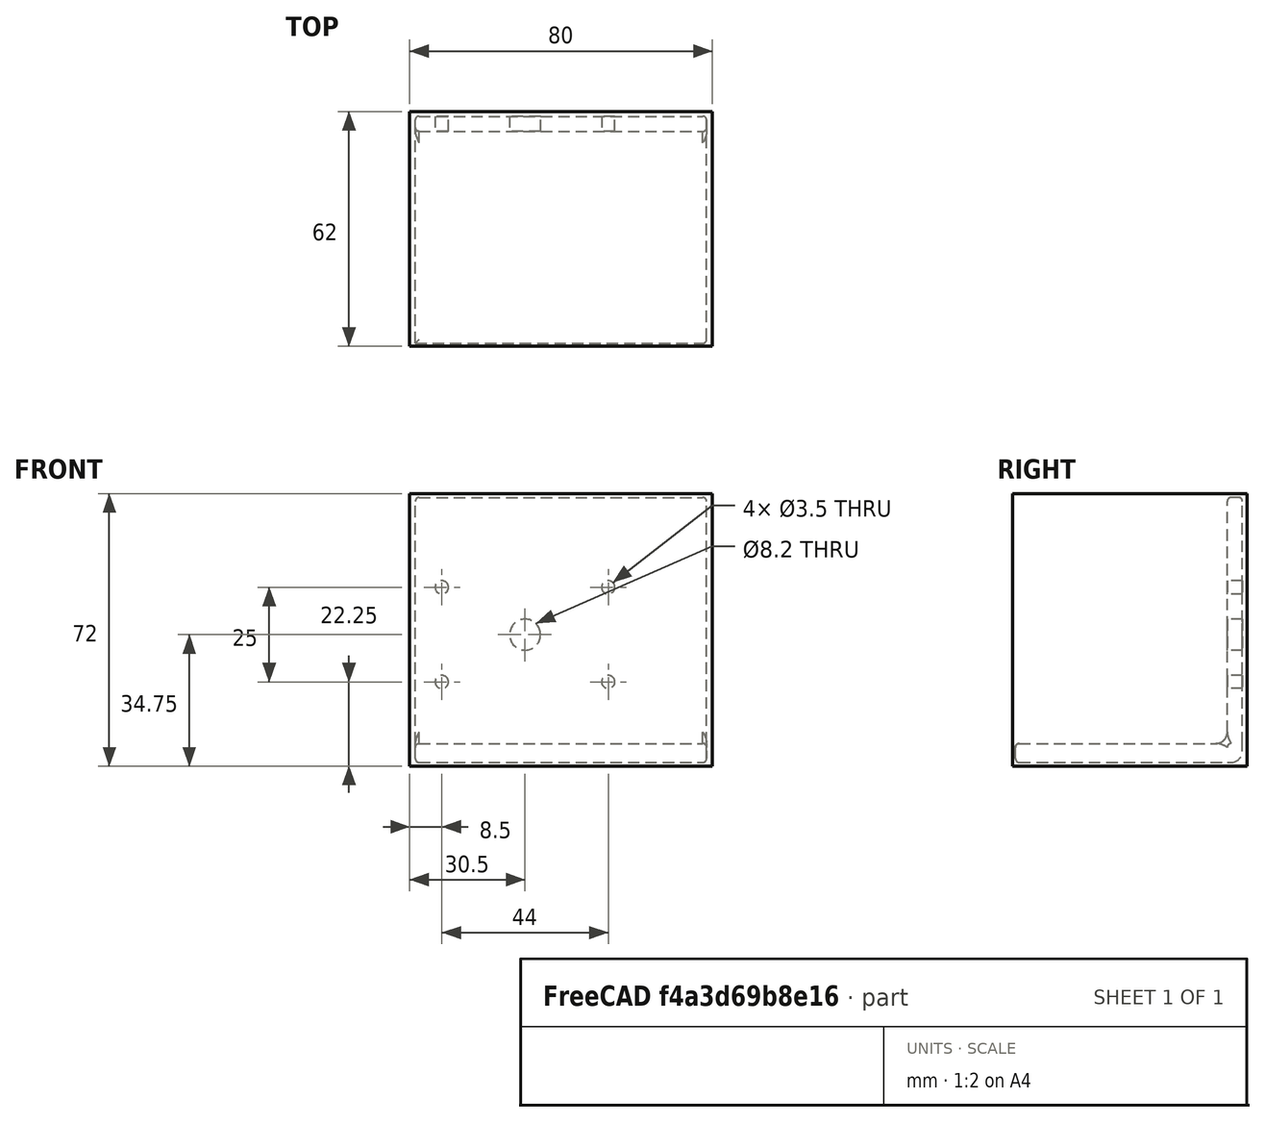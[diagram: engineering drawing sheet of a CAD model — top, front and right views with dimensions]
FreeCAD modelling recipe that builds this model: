
FCSTD DOCUMENT  (FreeCAD 0.21R33668 +7 (Git))
Label: OPC_N3_Base_July_10_2024
License: All rights reserved
LicenseURL: https://en.wikipedia.org/wiki/All_rights_reserved
objects: Part::Cylinder×5, Part::Box×3, Part::MultiFuse×2, Mesh::Feature×1, Part::Cut×1, Part::Fillet×1
note: 12 computed .brp shape members not serialized (recipe doc carries the construction recipe); baked Part::Feature solids carry a one-line shape summary decoded from their .brp

FEATURE [Mesh::Feature] opc_n3
FEATURE [Part::Box] Box  label="Horizontal"
  AttacherType = Attacher::AttachEngine3D
  Height = 5
  Length = 77
  Placement = pos=(-2.5,-31.25,-37) rot=(0,0,1;0rad)
  Width = 60
FEATURE [Part::Box] Box001  label="Vertical"
  AttacherType = Attacher::AttachEngine3D
  Height = 4
  Length = 77
  Placement = pos=(-2.5,28.75,-37) rot=(1,0,0;1.5708rad)
  Width = 70
FEATURE [Part::MultiFuse] Fusion  label="Plate"
  Shapes = -> [Box,Box001]
FEATURE [Part::Cylinder] Cylinder
  Angle = 360
  AttacherType = Attacher::AttachEngine3D
  FirstAngle = 0
  Height = 10
  Placement = pos=(26.5,22,-3.25) rot=(1,0,0;4.71239rad)
  Radius = 4.1
  SecondAngle = 0
FEATURE [Part::Cylinder] Cylinder001
  Angle = 360
  AttacherType = Attacher::AttachEngine3D
  FirstAngle = 0
  Height = 10
  Placement = pos=(48.5,22,9.25) rot=(-1,0,0;1.5708rad)
  Radius = 1.75
  SecondAngle = 0
FEATURE [Part::Cylinder] Cylinder003
  Angle = 360
  AttacherType = Attacher::AttachEngine3D
  FirstAngle = 0
  Height = 10
  Placement = pos=(4.5,22,-15.75) rot=(-1,0,0;1.5708rad)
  Radius = 1.75
  SecondAngle = 0
FEATURE [Part::Cylinder] Cylinder002
  Angle = 360
  AttacherType = Attacher::AttachEngine3D
  FirstAngle = 0
  Height = 10
  Placement = pos=(4.5,22,9.25) rot=(-1,0,0;1.5708rad)
  Radius = 1.75
  SecondAngle = 0
FEATURE [Part::Cylinder] Cylinder004
  Angle = 360
  AttacherType = Attacher::AttachEngine3D
  FirstAngle = 0
  Height = 10
  Placement = pos=(48.5,22,-15.75) rot=(-1,0,0;1.5708rad)
  Radius = 1.75
  SecondAngle = 0
FEATURE [Part::MultiFuse] Fusion001  label="Holes"
  Shapes = -> [Cylinder,Cylinder001,Cylinder002,Cylinder003,Cylinder004]
FEATURE [Part::Cut] Cut  label="Mount_Plate"
  Base = -> Fusion
  Tool = -> Fusion001
FEATURE [Part::Fillet] Fillet  label="MountPlate"
  Base = -> Cut
  Edges = 17 edges: [Edge1 r=1,Edge3 r=1,Edge5 r=3,Edge6 r=1,Edge7 r=1,Edge12 r=1,Edge13 r=1,Edge14 r=1,Edge15 r=1,Edge16 r=1,Edge17 r=1,Edge24 r=1,Edge25 r=1,Edge26 r=3,Edge30 r=1,Edge31 r=1,Edge32 r=1]
FEATURE [Part::Box] Box002  label="Volume"
  AttacherType = Attacher::AttachEngine3D
  Height = 72
  Length = 80
  Placement = pos=(-4,-32,-38) rot=(0,0,1;0rad)
  Width = 62
